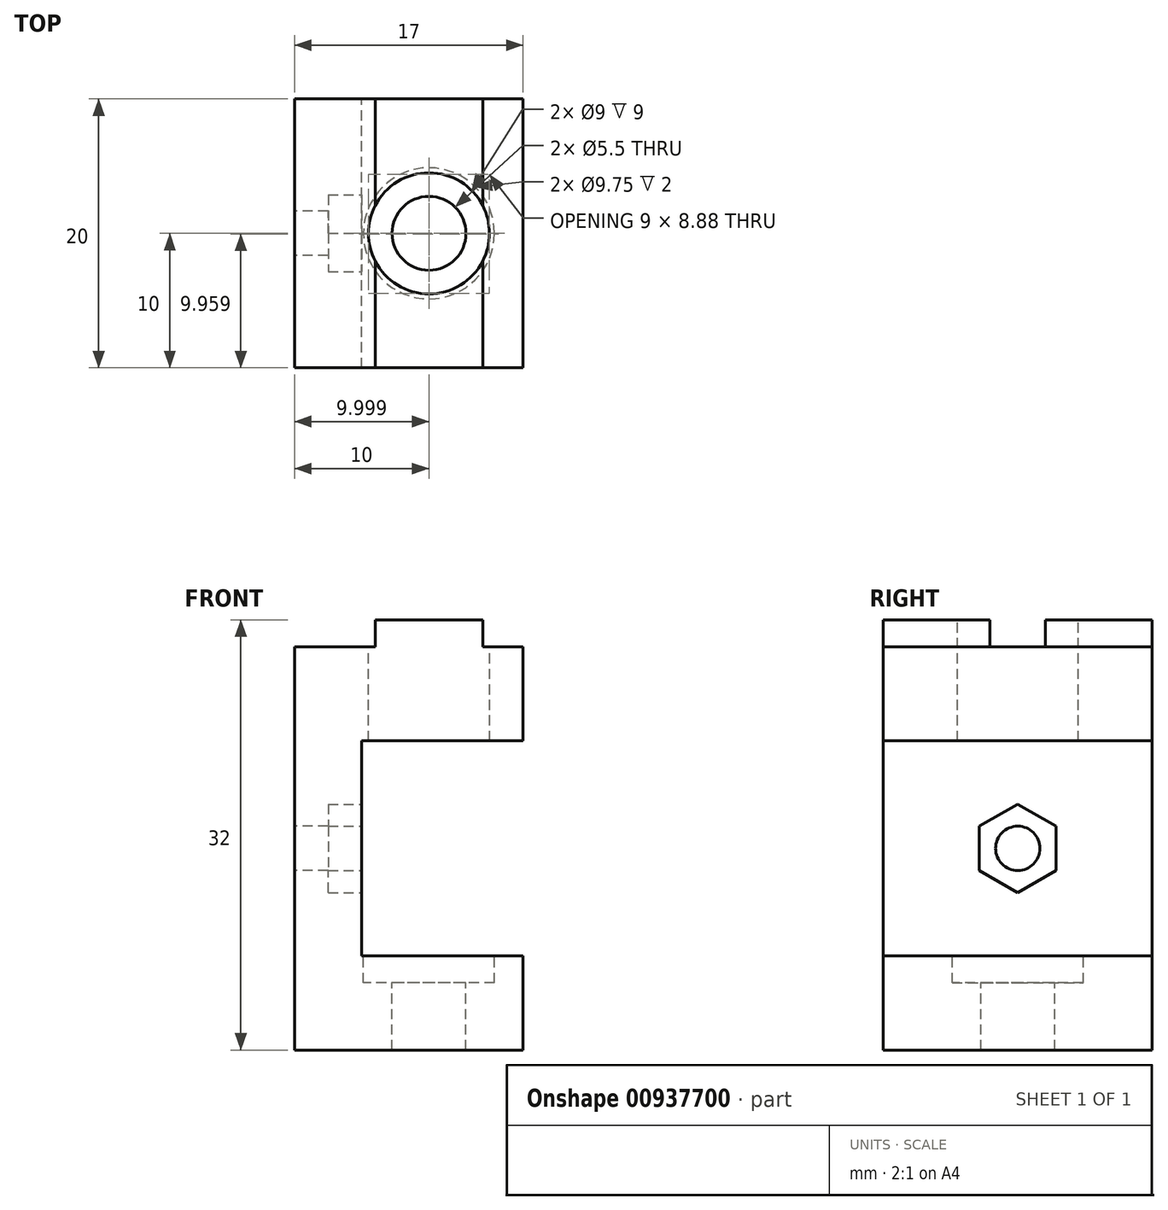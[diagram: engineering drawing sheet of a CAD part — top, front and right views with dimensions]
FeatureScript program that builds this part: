
annotation { "Feature Type Name" : "Feature", "Feature Type Description" : "" }
export const myFeature = defineFeature(function(context is Context, id is Id, definition is map)
    precondition{}
    {
        {
            var Q0;
            Q0=qCreatedBy(makeId("Front.planeOp"),FACE);
            var sketch = newSketch(context, id + "F0", { "sketchPlane" : qUnion([Q0])});
            skLineSegment(sketch, "E0.bottom", {"start": v(-15, -15) * mm, "end": v(15, -15) * mm});
            skLineSegment(sketch, "E0.top", {"start": v(-15, -45) * mm, "end": v(15, -45) * mm});
            skLineSegment(sketch, "E0.left", {"start": v(-15, -15) * mm, "end": v(-15, -45) * mm});
            skLineSegment(sketch, "E0.right", {"start": v(15, -15) * mm, "end": v(15, -45) * mm});
            skLineSegment(sketch, "E1.bottom", {"start": v(-15, 15) * mm, "end": v(15, 15) * mm});
            skLineSegment(sketch, "E1.top", {"start": v(-15, 45) * mm, "end": v(15, 45) * mm});
            skLineSegment(sketch, "E1.left", {"start": v(-15, 15) * mm, "end": v(-15, 45) * mm});
            skLineSegment(sketch, "E1.right", {"start": v(15, 15) * mm, "end": v(15, 45) * mm});
            skLineSegment(sketch, "E2.bottom", {"start": v(-13, 14.75) * mm, "end": v(-10, 14.75) * mm});
            skLineSegment(sketch, "E2.top", {"start": v(-13, -14.75) * mm, "end": v(-10, -14.75) * mm});
            skLineSegment(sketch, "E2.left", {"start": v(-13, 14.75) * mm, "end": v(-13, -14.75) * mm});
            skLineSegment(sketch, "E2.right", {"start": v(-10, 14.75) * mm, "end": v(-10, -14.75) * mm});
            skLineSegment(sketch, "E3.bottom", {"start": v(-4, 17) * mm, "end": v(4, 17) * mm});
            skLineSegment(sketch, "E3.top", {"start": v(-4, -22.99) * mm, "end": v(4, -22.99) * mm});
            skLineSegment(sketch, "E3.left", {"start": v(-4, 17) * mm, "end": v(-4, 15) * mm});
            skLineSegment(sketch, "E3.right", {"start": v(4, 17) * mm, "end": v(4, 15) * mm});
            skLineSegment(sketch, "E4.trimOffspring", {"start": v(-4, -15) * mm, "end": v(-4, -22.99) * mm});
            skLineSegment(sketch, "E5.trimOffspring", {"start": v(4, -15) * mm, "end": v(4, -22.99) * mm});
            skLineSegment(sketch, "E6", {"start": v(7, 15) * mm, "end": v(7, 8) * mm});
            skLineSegment(sketch, "E7", {"start": v(7, 8) * mm, "end": v(-5, 8) * mm});
            skLineSegment(sketch, "E8", {"start": v(-5, 8) * mm, "end": v(-5, -8) * mm});
            skLineSegment(sketch, "E9", {"start": v(-5, -8) * mm, "end": v(7, -8) * mm});
            skLineSegment(sketch, "E10", {"start": v(7, -8) * mm, "end": v(7, -15) * mm});
            skLineSegment(sketch, "E11", {"start": v(7, -15) * mm, "end": v(-10, -15) * mm});
            skLineSegment(sketch, "E12", {"start": v(-10, -15) * mm, "end": v(-10, -14.75) * mm});
            skLineSegment(sketch, "E13", {"start": v(-10, 14.75) * mm, "end": v(-10, 15) * mm});
            skSolve(sketch);
        }
        {
            var Q0;
            Q0=makeQuery(id+"F0.imprint","IMPRINT",FACE,{"disambiguationData":[TD([[makeQuery(id+"F0.imprint","IMPRINT",EDGE,{"derivedFrom":sQuery(id+"F0.wireOp",EDGE,"E2.right")}),1.0]])]});
            var Q1;
            Q1=makeQuery(id+"F0.imprint","IMPRINT",FACE,{"disambiguationData":[TD([[makeQuery(id+"F0.imprint","IMPRINT",EDGE,{"derivedFrom":sQuery(id+"F0.wireOp",EDGE,"E3.bottom")}),-1.0]])]});
            extrude(context, id + "F1", {"entities" : qUnion([Q0, Q1]), "endBound" : BoundingType.SYMMETRIC, "depth" : 20 * mm, "offsetDistance" : 25 * mm});
        }
        {
            var Q0;
            Q0=makeQuery(id+"F1.opExtrude","SWEPT_FACE",FACE,{"disambiguationData":[OSD([sQuery(id+"F0.wireOp",EDGE,"E3.bottom")])]});
            var sketch = newSketch(context, id + "F2", { "sketchPlane" : qUnion([Q0])});
            skCircle(sketch, "E14", {"center": v(0, 0) * mm, "radius": 4.5 * mm});
            skSolve(sketch);
        }
        {
            var Q0;
            {var subQ0=sQuery(id+"F2.wireOp",EDGE,"E14");var subQ1=makeQuery(id+"F1.opExtrude","SWEPT_EDGE",EDGE,{"disambiguationData":[OSD([sQuery(id+"F0.wireOp",EDGE,"E3.bottom"),sQuery(id+"F0.wireOp",EDGE,"E3.left")])]});var subQ2=makeQuery(id+"F2.imprint","INTERSECT",VERTEX,{"disambiguationData":[OD(0.0)],"derivedFrom":[subQ1,subQ0]});Q0=makeQuery(id+"F2.imprint","IMPRINT",FACE,{"disambiguationData":[TD([[makeQuery(id+"F2.imprint","IMPRINT",EDGE,{"disambiguationData":[TD([[subQ2,-1.0]])],"derivedFrom":subQ0}),1.0]])]});}
            var Q1;
            {var subQ0=sQuery(id+"F2.wireOp",EDGE,"E14");var subQ1=sQuery(id+"F0.wireOp",EDGE,"E3.bottom");var subQ2=makeQuery(id+"F1.opExtrude","SWEPT_EDGE",EDGE,{"disambiguationData":[OSD([subQ1,sQuery(id+"F0.wireOp",EDGE,"E3.left")])]});var subQ3=makeQuery(id+"F2.imprint","INTERSECT",VERTEX,{"disambiguationData":[OD(0.0)],"derivedFrom":[subQ2,subQ0]});Q1=makeQuery(id+"F2.imprint","IMPRINT",FACE,{"disambiguationData":[TD([[makeQuery(id+"F2.imprint","IMPRINT",EDGE,{"disambiguationData":[TD([[subQ3,1.0]])],"derivedFrom":subQ0}),1.0]])]});}
            var Q2;
            {var subQ0=sQuery(id+"F2.wireOp",EDGE,"E14");var subQ1=makeQuery(id+"F1.opExtrude","SWEPT_EDGE",EDGE,{"disambiguationData":[OSD([sQuery(id+"F0.wireOp",EDGE,"E3.bottom"),sQuery(id+"F0.wireOp",EDGE,"E3.right")])]});var subQ2=makeQuery(id+"F2.imprint","INTERSECT",VERTEX,{"disambiguationData":[OD(0.0)],"derivedFrom":[subQ1,subQ0]});Q2=makeQuery(id+"F2.imprint","IMPRINT",FACE,{"disambiguationData":[TD([[makeQuery(id+"F2.imprint","IMPRINT",EDGE,{"disambiguationData":[TD([[subQ2,1.0]])],"derivedFrom":subQ0}),1.0]])]});}
            extrude(context, id + "F3", {"entities" : qUnion([Q0, Q1, Q2]), "operationType" : NewBodyOperationType.REMOVE, "endBound" : BoundingType.UP_TO_NEXT, "oppositeDirection" : true, "depth" : 25 * mm, "offsetDistance" : 25 * mm});
        }
        {
            var Q0;
            Q0=makeQuery(id+"F1.opExtrude","SWEPT_FACE",FACE,{"disambiguationData":[OSD([sQuery(id+"F0.wireOp",EDGE,"E9")])]});
            var sketch = newSketch(context, id + "F4", { "sketchPlane" : qUnion([Q0])});
            skPoint(sketch, "E15", {"position": v(0, 0) * mm});
            skSolve(sketch);
        }
        {
            var Q0;
            Q0=sQuery(id+"F4.wireOp",VERTEX,"E15");
            var Q1;
            Q1=makeQuery(id+"F1.opExtrude","SWEPT_BODY",BODY,{"disambiguationData":[OSD([sQuery(id+"F0.wireOp",EDGE,"E1.bottom"),sQuery(id+"F0.wireOp",EDGE,"E2.right"),sQuery(id+"F0.wireOp",EDGE,"E3.bottom"),sQuery(id+"F0.wireOp",EDGE,"E3.left"),sQuery(id+"F0.wireOp",EDGE,"E3.right"),sQuery(id+"F0.wireOp",EDGE,"E6"),sQuery(id+"F0.wireOp",EDGE,"E7"),sQuery(id+"F0.wireOp",EDGE,"E8"),sQuery(id+"F0.wireOp",EDGE,"E9"),sQuery(id+"F0.wireOp",EDGE,"E10"),sQuery(id+"F0.wireOp",EDGE,"E11"),sQuery(id+"F0.wireOp",EDGE,"E12"),sQuery(id+"F0.wireOp",EDGE,"E13")])]});
            hole(context, id + "F5", {"style" : HoleStyle.C_BORE, "endStyle" : HoleEndStyle.BLIND, "holeDiameter" : 5.5 * mm, "cBoreDiameter" : 9.75 * mm, "cBoreDepth" : 2 * mm, "majorDiameter" : 5 * mm, "holeDepth" : 22 * mm, "isTappedThrough" : true, "tappedDepth" : 20 * mm, "tapClearance" : 3, "locations" : qUnion([Q0]), "scope" : qUnion([Q1])});
        }
        {
            var Q0;
            Q0=makeQuery(id+"F1.opExtrude","SWEPT_FACE",FACE,{"disambiguationData":[OSD([sQuery(id+"F0.wireOp",EDGE,"E2.right"),sQuery(id+"F0.wireOp",EDGE,"E12"),sQuery(id+"F0.wireOp",EDGE,"E13")])]});
            var sketch = newSketch(context, id + "F6", { "sketchPlane" : qUnion([Q0])});
            skPoint(sketch, "E16", {"position": v(0, 0) * mm});
            skSolve(sketch);
        }
        {
            var Q0;
            Q0=sQuery(id+"F6.wireOp",VERTEX,"E16");
            var Q1;
            Q1=makeQuery(id+"F1.opExtrude","SWEPT_BODY",BODY,{"disambiguationData":[OSD([sQuery(id+"F0.wireOp",EDGE,"E1.bottom"),sQuery(id+"F0.wireOp",EDGE,"E2.right"),sQuery(id+"F0.wireOp",EDGE,"E3.bottom"),sQuery(id+"F0.wireOp",EDGE,"E3.left"),sQuery(id+"F0.wireOp",EDGE,"E3.right"),sQuery(id+"F0.wireOp",EDGE,"E6"),sQuery(id+"F0.wireOp",EDGE,"E7"),sQuery(id+"F0.wireOp",EDGE,"E8"),sQuery(id+"F0.wireOp",EDGE,"E9"),sQuery(id+"F0.wireOp",EDGE,"E10"),sQuery(id+"F0.wireOp",EDGE,"E11"),sQuery(id+"F0.wireOp",EDGE,"E12"),sQuery(id+"F0.wireOp",EDGE,"E13")])]});
            hole(context, id + "F7", {"style" : HoleStyle.SIMPLE, "endStyle" : HoleEndStyle.BLIND, "holeDiameter" : 3.3 * mm, "majorDiameter" : 5 * mm, "holeDepth" : 22 * mm, "isTappedThrough" : true, "tappedDepth" : 20 * mm, "tapClearance" : 3, "locations" : qUnion([Q0]), "scope" : qUnion([Q1])});
        }
        {
            var Q0;
            Q0=makeQuery(id+"F1.opExtrude","SWEPT_FACE",FACE,{"disambiguationData":[OSD([sQuery(id+"F0.wireOp",EDGE,"E8")])]});
            var sketch = newSketch(context, id + "F8", { "sketchPlane" : qUnion([Q0])});
            skCircle(sketch, "E17.cCircle", {"center": v(0, 0) * mm, "radius": 2.85 * mm, "construction": true});
            skLineSegment(sketch, "E17.0", {"start": v(-2.85, -1.65) * mm, "end": v(-2.85, 1.65) * mm});
            skLineSegment(sketch, "E17.1", {"start": v(-2.85, 1.65) * mm, "end": v(0, 3.3) * mm});
            skLineSegment(sketch, "E17.2", {"start": v(0, 3.3) * mm, "end": v(2.85, 1.65) * mm});
            skLineSegment(sketch, "E17.3", {"start": v(2.85, 1.65) * mm, "end": v(2.85, -1.65) * mm});
            skLineSegment(sketch, "E17.4", {"start": v(2.85, -1.65) * mm, "end": v(0, -3.3) * mm});
            skLineSegment(sketch, "E17.5", {"start": v(0, -3.3) * mm, "end": v(-2.85, -1.65) * mm});
            skPoint(sketch, "E17.0.midPoint", {"position": v(-2.85, 0) * mm});
            skSolve(sketch);
        }
        {
            var Q0;
            Q0=makeQuery(id+"F8.imprint","IMPRINT",FACE,{"disambiguationData":[TD([[makeQuery(id+"F8.imprint","IMPRINT",EDGE,{"derivedFrom":sQuery(id+"F8.wireOp",EDGE,"E17.0")}),-1.0]])]});
            extrude(context, id + "F9", {"entities" : qUnion([Q0]), "operationType" : NewBodyOperationType.REMOVE, "oppositeDirection" : true, "depth" : 2.5 * mm, "offsetDistance" : 25 * mm});
        }
    });
